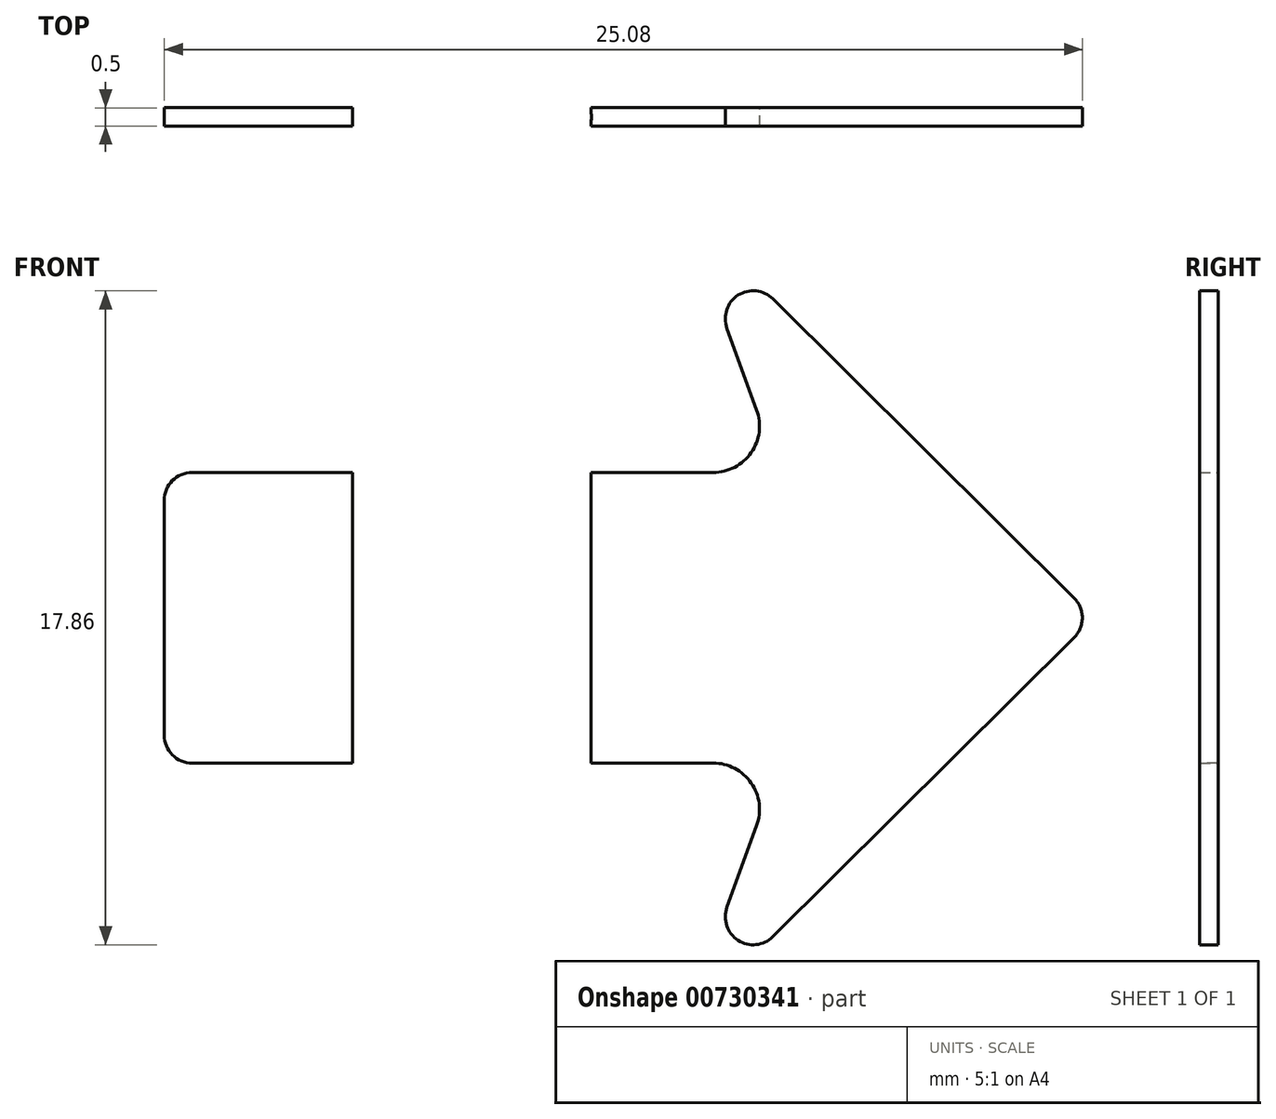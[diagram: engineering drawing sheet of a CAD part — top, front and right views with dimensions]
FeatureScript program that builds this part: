
annotation { "Feature Type Name" : "Feature", "Feature Type Description" : "" }
export const myFeature = defineFeature(function(context is Context, id is Id, definition is map)
    precondition{}
    {
        {
            assignVariable(context, id + "F0", {"name" : "Drill_F", "anyValue" : .257});
        }
        {
            assignVariable(context, id + "F1", {"name" : "WallMin", "anyValue" : 1 / 8});
        }
        {
            var Q0;
            Q0=qCreatedBy(makeId("Front.planeOp"),FACE);
            var sketch = newSketch(context, id + "F2", { "sketchPlane" : qUnion([Q0])});
            skLineSegment(sketch, "E0", {"start": v(0, 0) * mm, "end": v(8.4, 0) * mm});
            skLineSegment(sketch, "E1", {"start": v(5.8, -15.08) * mm, "end": v(17, -3.97) * mm});
            skLineSegment(sketch, "E2", {"start": v(17, -3.97) * mm, "end": v(5.8, 7.14) * mm});
            skLineSegment(sketch, "E3", {"start": v(8.4, -7.94) * mm, "end": v(-8.4, -7.94) * mm});
            skLineSegment(sketch, "E4", {"start": v(-8.4, 0) * mm, "end": v(-8.4, -7.94) * mm});
            skLineSegment(sketch, "E5", {"start": v(-8.4, 0) * mm, "end": v(0, 0) * mm});
            skLineSegment(sketch, "E6", {"start": v(8.4, -7.94) * mm, "end": v(8.4, 0) * mm, "construction": true});
            skLineSegment(sketch, "E7", {"start": v(8.4, 0) * mm, "end": v(5.8, 7.14) * mm});
            skLineSegment(sketch, "E8", {"start": v(8.4, -7.94) * mm, "end": v(5.8, -15.08) * mm});
            skLineSegment(sketch, "E9", {"start": v(17, -3.97) * mm, "end": v(8.4, -3.97) * mm, "construction": true});
            skLineSegment(sketch, "E10", {"start": v(-3.26, 0) * mm, "end": v(-3.26, -7.94) * mm, "construction": true});
            skLineSegment(sketch, "E11", {"start": v(3.26, 0) * mm, "end": v(3.26, -7.94) * mm, "construction": true});
            skLineSegment(sketch, "E12", {"start": v(0, 0) * mm, "end": v(0, -7.94) * mm, "construction": true});
            skSolve(sketch);
        }
        {
            var Q0;
            Q0=makeQuery(id+"F2.imprint","IMPRINT",FACE,{"disambiguationData":[TD([[makeQuery(id+"F2.imprint","IMPRINT",EDGE,{"derivedFrom":sQuery(id+"F2.wireOp",EDGE,"E0")}),-1.0]])]});
            extrude(context, id + "F3", {"entities" : qUnion([Q0]), "endBound" : BoundingType.SYMMETRIC, "depth" : (getVariable(context, 'Drill_F') + 2 * getVariable(context, 'WallMin')) * mm, "offsetDistance" : 25.4 * mm});
        }
        {
            var Q0;
            Q0=makeQuery(id+"F3.opExtrude","SWEPT_FACE",FACE,{"disambiguationData":[OSD([sQuery(id+"F2.wireOp",EDGE,"E0"),sQuery(id+"F2.wireOp",EDGE,"E5")])]});
            var sketch = newSketch(context, id + "F4", { "sketchPlane" : qUnion([Q0])});
            skCircle(sketch, "E13", {"center": v(0, 0) * mm, "radius": 3.26 * mm});
            skSolve(sketch);
        }
        {
            var Q0;
            Q0=makeQuery(id+"F4.imprint","IMPRINT",FACE,{"disambiguationData":[TD([[makeQuery(id+"F4.imprint","IMPRINT",EDGE,{"derivedFrom":sQuery(id+"F4.wireOp",EDGE,"E13")}),1.0]])]});
            extrude(context, id + "F5", {"entities" : qUnion([Q0]), "operationType" : NewBodyOperationType.REMOVE, "oppositeDirection" : true, "depth" : 25.4 * mm, "offsetDistance" : 25.4 * mm});
        }
        {
            var Q0;
            Q0=makeQuery(id+"F3.opExtrude","SWEPT_EDGE",EDGE,{"disambiguationData":[OSD([sQuery(id+"F2.wireOp",EDGE,"E0"),sQuery(id+"F2.wireOp",EDGE,"E7")])]});
            var Q1;
            Q1=makeQuery(id+"F3.opExtrude","SWEPT_EDGE",EDGE,{"disambiguationData":[OSD([sQuery(id+"F2.wireOp",EDGE,"E3"),sQuery(id+"F2.wireOp",EDGE,"E8")])]});
            fillet(context, id + "F6", {"entities" : qUnion([Q0, Q1]), "radius" : 1.27 * mm, "tangentPropagation" : true, "allowEdgeOverflow" : false});
        }
        {
            var Q0;
            Q0=makeQuery(id+"F6.opFillet","BLEND_EDGE",EDGE,{"blendedFrom":[makeQuery(id+"F3.opExtrude","SWEPT_EDGE",EDGE,{"disambiguationData":[OSD([sQuery(id+"F2.wireOp",EDGE,"E0"),sQuery(id+"F2.wireOp",EDGE,"E7")])]}),makeQuery(id+"F3.opExtrude","SWEPT_FACE",FACE,{"disambiguationData":[OSD([sQuery(id+"F2.wireOp",EDGE,"E2")])]})],"blendedInto":[makeQuery(id+"F3.opExtrude","SWEPT_FACE",FACE,{"disambiguationData":[OSD([sQuery(id+"F2.wireOp",EDGE,"E2")])]})]});
            var Q1;
            Q1=makeQuery(id+"F6.opFillet","BLEND_EDGE",EDGE,{"blendedFrom":[makeQuery(id+"F3.opExtrude","SWEPT_EDGE",EDGE,{"disambiguationData":[OSD([sQuery(id+"F2.wireOp",EDGE,"E3"),sQuery(id+"F2.wireOp",EDGE,"E8")])]}),makeQuery(id+"F3.opExtrude","SWEPT_FACE",FACE,{"disambiguationData":[OSD([sQuery(id+"F2.wireOp",EDGE,"E1")])]})],"blendedInto":[makeQuery(id+"F3.opExtrude","SWEPT_FACE",FACE,{"disambiguationData":[OSD([sQuery(id+"F2.wireOp",EDGE,"E1")])]})]});
            var Q2;
            Q2=makeQuery(id+"F3.opExtrude","SWEPT_EDGE",EDGE,{"disambiguationData":[OSD([sQuery(id+"F2.wireOp",EDGE,"E1"),sQuery(id+"F2.wireOp",EDGE,"E2")])]});
            var Q3;
            Q3=makeQuery(id+"F3.opExtrude","SWEPT_EDGE",EDGE,{"disambiguationData":[OSD([sQuery(id+"F2.wireOp",EDGE,"E4"),sQuery(id+"F2.wireOp",EDGE,"E5")])]});
            var Q4;
            Q4=makeQuery(id+"F3.opExtrude","SWEPT_EDGE",EDGE,{"disambiguationData":[OSD([sQuery(id+"F2.wireOp",EDGE,"E3"),sQuery(id+"F2.wireOp",EDGE,"E4")])]});
            var Q5;
            Q5=makeQuery(id+"F3.opExtrude","SWEPT_EDGE",EDGE,{"disambiguationData":[OSD([sQuery(id+"F2.wireOp",EDGE,"E2"),sQuery(id+"F2.wireOp",EDGE,"E7")])]});
            var Q6;
            Q6=makeQuery(id+"F3.opExtrude","SWEPT_EDGE",EDGE,{"disambiguationData":[OSD([sQuery(id+"F2.wireOp",EDGE,"E1"),sQuery(id+"F2.wireOp",EDGE,"E8")])]});
            fillet(context, id + "F7", {"entities" : qUnion([Q0, Q1, Q2, Q3, Q4, Q5, Q6]), "radius" : 0.76 * mm, "tangentPropagation" : true, "allowEdgeOverflow" : false});
        }
    });
